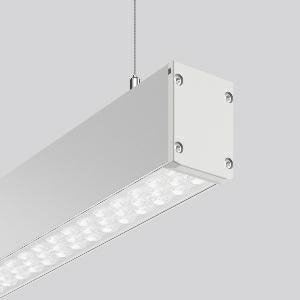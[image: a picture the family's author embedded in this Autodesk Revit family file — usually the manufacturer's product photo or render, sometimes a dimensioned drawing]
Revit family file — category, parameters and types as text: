
# Revit family: linedo_single_ip54_312565_000_1_adb7
name_source: partatom
category: Lighting Fixtures
units: mm (PartAtom-declared; Revit-internal decimal feet)

## family parameters
Cut with Voids When Loaded = No
Host = Face
Light Source = No
Part Type = Normal
Room Calculation Point = No
Round Connector Dimension = Use Diameter
Shared = No

## types (1)
- LINEDO single IP54 (1 x LED Modul 840, 4850 lm, 4000)
    Apparent Load = 31 VA
    CIE Flux Codes = 86 96 99 100 100
    Color Rendering = 80
    Color Temperature = 4000
    Default Elevation = 1800 mm
    Description = Series: LINEDO single IP54
Stylish pendant luminaire. High-efficiency LED units with optimum light control thanks to clear plastic (PC) lens optics. 2-point steel cable suspension freely positionable and infinitely height-adjustable. With power cord (2.5 m). Please order canopy separately if required. Perfect for office areas (RUG < 19) and environments with computer screens in accordance with EN 12464-1. Luminaire with limited surface temperature in accordance with EN 60598-2-24 for use in environments in which a deposit of conductive dust on the luminaire can be expected. 
Colour: anodised aluminium
Length: 1710 mm
Width: 58 mm
Height: 76 mm
Suspension length: 100-1500 mm
Lamp: LED
Socket: without socket
Colour temperature: 4000K
Colour rendering index (CRI): 80
System power: 31 W
Rated luminous flux: 4850 lm
Beam angle Down: 59°
Luminous efficiency: 156 lm/W
Control gear: Regulated power supply
Protection class: I
Type of protection: IP 54
    Height = 76 mm
    Lamp = 1 x LED Modul 840
    Lamp Light Flux = 4850 lm
    Lamp count = 1
    Length = 1710 mm
    Lifetime = 50000 h
    Luminous efficacy = 156 lm/W
    Manufacturer = RZB
    ModVariant = No
    Model = 312565.000.1
    Mounting Place = Ceiling
    Mounting Type = Pendant
    Number of Poles = 1
    OnlyDefault = Yes
    Power Factor = 1
    Product Name = LINEDO single IP54
    Product group = Pendant luminaires
    ProductGroupID = 902
    Protection Class = Protection class I
    Protection Degree = Degree of protection
    RLX_Detail_Level = 1
    RLX_Emergency_Light_Flux = 0 lm
    RLX_Emergency_Type = 0
    RLX_Emergency_Type_DB = No
    RlxData = <blob elided: 30781 chars, md5=dd605adf>
    Socket = socket
    Standby Power = 0 W
    System Light Flux = 4850 lm
    System Power = 31 W
    Type Comments = ALEA SPOT
    Type Image = 312565.000.jpg
    URL = http://relux.com
    VarID = ---
    Voltage = 0 V
    Weight = 0.00 kg
    Width = 58 mm

## geometry (parser evidence)
native form markers: Blend x4, Sweep x12
no freeform markers — native parametric forms only
